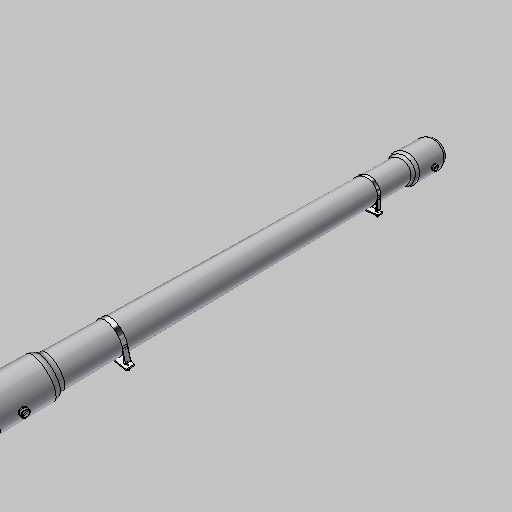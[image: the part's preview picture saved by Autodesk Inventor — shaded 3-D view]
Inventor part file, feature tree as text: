
AUTODESK INVENTOR PART (.ipt)
format: ipt  version: 2025.2 (Build 292293000, 293)  size: 463,360 bytes
history: native  units: mm
features: other x11, extrude x7, mirror x5, plane x2, pattern_linear x2, sketch x1, hole x1, revolve x1
ambient origin geometry x8: Origin, YZ Plane, XZ Plane, XY Plane, X Axis, Y Axis, Z Axis, Center Point
bodies: Solid5 (feature_tree), Solid6 (feature_tree), Solid7 (feature_tree), Solid8 (feature_tree), Solid9 (feature_tree), Solid10 (feature_tree), Solid11 (feature_tree)
feature tree (30):
  plane  "Work Plane4"
  sketch  "Sketch3"  dims[d14=3532.0mm d15=217.0mm d16=50.0mm d17=400.0mm d18=264.0mm d19=56.0mm d20=63.0mm d21=48.2mm d22=3.68mm d23=106.5mm d24=15.88mm d25=7.95mm d26=45.09mm d27=48.3mm d28=3.68mm d33=48.3mm d34=152.0mm d35=33.7mm d36=25.0mm d38=4.0mm d39=64.0mm d40=1.0mm d41=152.0mm d44=90.0deg d45=90.0deg d46=90.0deg d47=90.0deg d48=20.0mm d50=3200.0mm d51=90.0deg d52=90.0deg d53=90.0deg d54=90.0deg d55=0.0mm d56=0.0mm d57=0.0mm d58=0.0mm d59=0.0mm d60=0.0mm d61=-1016.0mm d62=2.0mm d63=6.0mm d64=1.0mm d65=125.0mm d66=229.0mm d67=30.0mm d69=270.0mm d70=10.0mm d71=150.0mm d72=32.0mm d73=0.0mm d74=32.0mm d75=0.0mm d76=52.0mm d77=0.0mm d78=10.0mm d79=6.0mm d80=4.0mm d81=2.0mm d82=90.0deg d83=30.0mm d84=20.594885mm d85=40.0mm d86=0.0mm d87=8.0mm d88=15.0mm d89=0.0mm d90=13.0mm d91=8.0mm d92=0.0mm d93=35.0mm d94=0.0mm d95=20.0mm d97=2032.0mm d105=206.0mm d107=200.0mm d109=90.0deg d110=101.0mm]
  other  "Corps"
  other  "BellPermeateSide"
  mirror  "BellBackSide"
  other  "Inside"
  other  "ConcentrateSideNozzle"
  pattern_linear  "FeedSideNozzle"  Spacing1=217.0mm  [1 undecoded]
  other  "ConcentrateEndNozzle"
  mirror  "FeedEndNozzle"
  other  "PermeateNozzle"
  other  "MaleTRD"
  other  "FemaleTRD"
  mirror  "Mirror3"
  plane  "Work Plane2"
  extrude  "Extrusion1"  Depth=50.0mm
  extrude  "Extrusion2"  Depth=101.0mm
  extrude  "Extrusion4"  Depth=101.0mm
  mirror  "Mirror4"
  extrude  "Extrusion3"  Depth=101.0mm
  hole  "Hole1"  [1 undecoded]
  extrude  "Extrusion5"  Depth=101.0mm
  extrude  "Extrusion6"  Depth=15.88mm
  extrude  "Extrusion7"  Depth=7.95mm
  mirror  "Mirror5"
  pattern_linear  "Rectangular Pattern2"  Spacing1=45.09mm  [1 undecoded]
  revolve  "Revolution11"  [1 undecoded]
  other  "Pattern of Solid5:1"
  other  "Pattern of Solid7:2"
  other  "Pattern of Solid9:3"
note: 4 required parameter values undecoded (feature->parameter linkage not recoverable at this tier; creation-order binding heuristic only, values carry confidence <= 0.55)